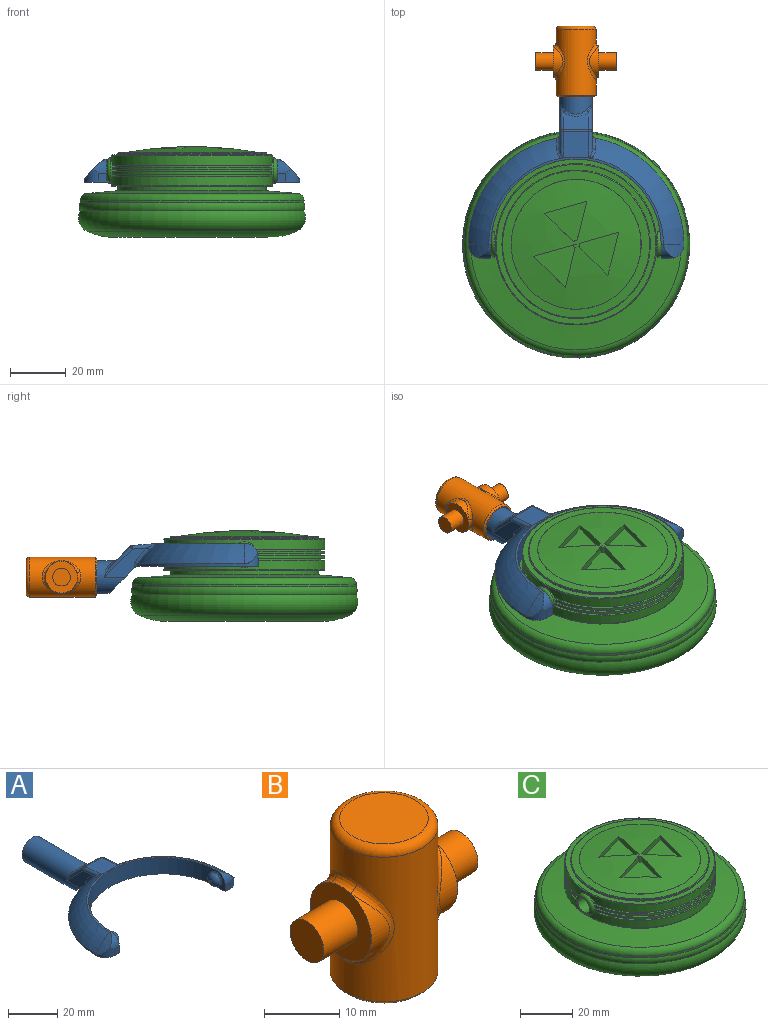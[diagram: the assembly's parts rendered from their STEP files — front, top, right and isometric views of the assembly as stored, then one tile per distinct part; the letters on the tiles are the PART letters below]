
ASSEMBLY  parts=3 mates=2
PART A: 48 faces, bbox 77.3x80.8x18.2 mm
  f0: plane 11.99x9.83mm, normal (0,-0.71,-0.71), area 141.5mm2, adj f1,f2,f9,f30,f43,f46
  f1: plane 15.39x10.49mm, normal (-1,0,0), area 63.5mm2, adj f0,f30,f32,f36,f46,f47
  f2: plane 15.39x10.49mm, normal (1,0,0), area 63.5mm2, adj f0,f30,f34,f39,f43,f44
  f3: plane 9.14x6.37mm, normal (0,0.71,0.71), area 67.6mm2, adj f35,f36,f39,f40
  f4: cylinder r=38.61mm len=37.99mm, axis (0,0,-1), area 42.6mm2, adj f6,f9,f17,f46,f47
  f5: torus R=19.3mm, axis (0,0,-1), area 507.8mm2, adj f10,f11,f12,f29,f42,f44
  f6: torus R=19.3mm, axis (0,0,-1), area 507.8mm2, adj f4,f11,f15,f28,f45,f47
  f7: cylinder r=30.48mm len=60.96mm, axis (0,0,-1), area 746.6mm2, adj f8,f9,f11,f14,f21,f24
  f8: plane 8.13x5.08mm, normal (-1,0,0), area 19.9mm2, adj f7,f9,f13,f19,f24
  f9: plane 77.22x43.73mm, normal (0,0,-1), area 956.2mm2, adj f0,f4,f7,f8,f10,f13,f14,f16
  f10: cylinder r=38.61mm len=37.99mm, axis (0,0,-1), area 42.6mm2, adj f5,f9,f20,f43,f44
  f11: plane 62.55x30.95mm, normal (0,0,1), area 75mm2, adj f5,f6,f7,f18,f19,f27
  f12: cylinder r=22.71mm len=7.33mm, axis (0,1,0), area 24.8mm2, adj f5,f19,f20
  f13: plane 3.05x3.05mm, normal (0,-1,0), area 9.3mm2, adj f8,f9,f19,f20
  f14: plane 8.13x5.08mm, normal (1,0,0), area 19.9mm2, adj f7,f9,f16,f18,f21
  f15: cylinder r=22.71mm len=7.33mm, axis (0,1,0), area 24.8mm2, adj f6,f17,f18
  f16: plane 3.05x3.05mm, normal (0,-1,0), area 9.3mm2, adj f9,f14,f17,f18
  f17: cylinder r=5.08mm len=5.08mm, axis (0,0,-1), area 21.9mm2, adj f4,f9,f15,f16,f18
  f18: cylinder r=5.08mm len=5.08mm, axis (-1,0,0), area 21.9mm2, adj f11,f14,f15,f16,f17
  f19: cylinder r=5.08mm len=5.08mm, axis (-1,0,0), area 21.9mm2, adj f8,f11,f12,f13,f20
  f20: cylinder r=5.08mm len=5.08mm, axis (0,0,-1), area 21.9mm2, adj f9,f10,f12,f13,f19
  f21: cylinder r=3.17mm len=6.35mm, axis (-1,0,0), area 12.7mm2, adj f7,f14,f23
  f22: plane 1.27x1.27mm, normal (1,0,0), area 1.3mm2, adj f23
  f23: torus R=0.64mm, axis (1,0,0), area 56.5mm2, adj f21,f22
  f24: cylinder r=3.17mm len=6.35mm, axis (1,0,0), area 12.7mm2, adj f7,f8,f26
  f25: plane 1.27x1.27mm, normal (-1,0,0), area 1.3mm2, adj f26
  f26: torus R=0.64mm, axis (-1,0,0), area 56.5mm2, adj f24,f25
  f27: plane 9.86x9.36mm, normal (0,0.09,1), area 85.6mm2, adj f11,f28,f29,f32,f34,f35,f42,f45
  f28: plane 1.04x0.17mm, normal (0,-1,0), area 0mm2, adj f6,f27,f45
  f29: plane 1.04x0.17mm, normal (0,-1,0), area 0mm2, adj f5,f27,f42
  f30: cylinder r=5.84mm len=33.01mm, axis (0,-1,0), area 1029.7mm2, adj f0,f1,f2,f31,f38,f40,f41
  f31: plane 11.68x11.68mm, normal (0,1,0), area 107.2mm2, adj f30
  f32: cylinder r=1.27mm len=9.13mm, axis (0,-1,0.09), area 14.4mm2, adj f1,f27,f33,f45
  f33: sphere r=1.27mm, area 1.5mm2, adj f32,f35,f36
  f34: cylinder r=1.27mm len=9.13mm, axis (0,1,-0.09), area 14.4mm2, adj f2,f27,f37,f42
  f35: cylinder r=1.27mm len=9.14mm, axis (-1,0,0), area 8.1mm2, adj f3,f27,f33,f37
  f36: cylinder r=1.27mm len=10.91mm, axis (0,-0.71,0.71), area 23.1mm2, adj f1,f3,f33,f38
  f37: sphere r=1.27mm, area 1.5mm2, adj f34,f35,f39
  f38: bspline ~4.55x2.75mm, area 2.3mm2, adj f30,f36,f40
  f39: cylinder r=1.27mm len=10.91mm, axis (0,0.71,-0.71), area 23.1mm2, adj f2,f3,f37,f41
  f40: bspline ~9.14x2.56mm, area 10.7mm2, adj f3,f30,f38,f41
  f41: bspline ~5.23x3.53mm, area 2.3mm2, adj f30,f39,f40
  f42: bspline ~4.62x3.14mm, area 5.2mm2, adj f5,f27,f29,f34,f44
  f43: cylinder r=1.27mm len=1.74mm, axis (0,0,-1), area 1.9mm2, adj f0,f2,f9,f10,f44
  f44: bspline ~8.6x7.86mm, area 11.9mm2, adj f2,f5,f10,f42,f43
  f45: bspline ~4.62x3.14mm, area 5.2mm2, adj f6,f27,f28,f32,f47
  f46: cylinder r=1.27mm len=1.74mm, axis (0,0,-1), area 1.9mm2, adj f0,f1,f4,f9,f47
  f47: bspline ~8.6x7.86mm, area 11.9mm2, adj f1,f4,f6,f45,f46
PART B: 25 faces, bbox 28.9x15.5x25.4 mm
  f0: cylinder r=5.71mm len=10.81mm, axis (-1,0,0), area 26.2mm2, adj f5,f15
  f1: cylinder r=5.71mm len=10.81mm, axis (-1,0,0), area 26.2mm2, adj f8,f11
  f2: cylinder r=7.14mm len=23.5mm, axis (0,0,-1), area 763.2mm2, adj f9,f10,f11,f12,f13,f14,f15,f16
  f3: plane 11.75x11.75mm, normal (0,0,1), area 108.4mm2, adj f17
  f4: plane 13.02x13.02mm, normal (0,0,-1), area 16.3mm2, adj f22,f24
  f5: plane 11.46x11.46mm, normal (1,0,0), area 70.9mm2, adj f0,f6,f13,f16,f18
  f6: cylinder r=5.71mm len=10.81mm, axis (-1,0,0), area 26.2mm2, adj f5,f14
  f7: cylinder r=5.71mm len=10.81mm, axis (-1,0,0), area 26.2mm2, adj f8,f10
  f8: plane 11.46x11.46mm, normal (-1,0,0), area 70.9mm2, adj f1,f7,f9,f12,f20
  f9: bspline ~4.64x1.73mm, area 6.5mm2, adj f2,f8,f10,f11
  f10: bspline ~13.62x4.91mm, area 20.7mm2, adj f2,f7,f9,f12
  f11: bspline ~13.6x4.87mm, area 20.7mm2, adj f1,f2,f9,f12
  f12: bspline ~4.64x1.73mm, area 6.5mm2, adj f2,f8,f10,f11
  f13: bspline ~4.64x1.73mm, area 6.5mm2, adj f2,f5,f14,f15
  f14: bspline ~13.62x4.91mm, area 20.7mm2, adj f2,f6,f13,f16
  f15: bspline ~13.6x4.87mm, area 20.7mm2, adj f0,f2,f13,f16
  f16: bspline ~4.64x1.73mm, area 6.5mm2, adj f2,f5,f14,f15
  f17: torus R=5.87mm, axis (0,0,1), area 83.8mm2, adj f2,f3
  f18: cylinder r=3.17mm len=6.35mm, axis (-1,0,0), area 126.7mm2, adj f5,f19
  f19: plane 6.35x6.35mm, normal (1,0,0), area 31.7mm2, adj f18
  f20: cylinder r=3.17mm len=6.35mm, axis (1,0,0), area 126.7mm2, adj f8,f21
  f21: plane 6.35x6.35mm, normal (-1,0,0), area 31.7mm2, adj f20
  f22: cylinder r=6.1mm len=22.86mm, axis (0,0,-1), area 875.6mm2, adj f4,f23
  f23: plane 12.19x12.19mm, normal (0,0,-1), area 116.7mm2, adj f22
  f24: cone r=7.14mm half-angle=45deg, axis (0,0,1), area 38.5mm2, adj f2,f4
PART C: 64 faces, bbox 96.3x96.3x32.5 mm
  f0: cylinder r=28.87mm len=57.73mm, axis (0,0,-1), area 595.8mm2, adj f1,f2,f54,f55,f60
  f1: plane 57.13x24.71mm, normal (0,0,1), area 102.4mm2, adj f0,f6,f54,f55
  f2: plane 57.13x24.71mm, normal (0,0,1), area 102.4mm2, adj f0,f5,f54,f55
  f3: plane 57.06x24.48mm, normal (0,0,-1), area 101.8mm2, adj f5,f7,f54,f55
  f4: plane 57.06x24.48mm, normal (0,0,-1), area 101.8mm2, adj f6,f8,f54,f55
  f5: cylinder r=27.59mm len=54.55mm, axis (0,0,-1), area 49.6mm2, adj f2,f3,f54,f55
  f6: cylinder r=27.59mm len=54.55mm, axis (0,0,-1), area 49.6mm2, adj f1,f4,f54,f55
  f7: cylinder r=28.87mm len=57.06mm, axis (0,0,-1), area 75.7mm2, adj f3,f10,f54,f55
  f8: cylinder r=28.87mm len=57.06mm, axis (0,0,-1), area 75.7mm2, adj f4,f9,f54,f55
  f9: plane 57.01x24.31mm, normal (0,0,1), area 101.4mm2, adj f8,f14,f54,f55
  f10: plane 57.01x24.31mm, normal (0,0,1), area 101.4mm2, adj f7,f13,f54,f55
  f11: plane 57.01x24.3mm, normal (0,0,-1), area 101.4mm2, adj f14,f16,f54,f55
  f12: plane 57.01x24.3mm, normal (0,0,-1), area 101.4mm2, adj f13,f15,f54,f55
  f13: cylinder r=27.59mm len=54.43mm, axis (0,0,-1), area 49.2mm2, adj f10,f12,f54,f55
  f14: cylinder r=27.59mm len=54.43mm, axis (0,0,-1), area 49.2mm2, adj f9,f11,f54,f55
  f15: cylinder r=28.87mm len=57.06mm, axis (0,0,-1), area 80mm2, adj f12,f19,f54,f55
  f16: cylinder r=28.87mm len=57.06mm, axis (0,0,-1), area 80mm2, adj f11,f20,f54,f55
  f17: plane 57.13x24.71mm, normal (0,0,-1), area 102.4mm2, adj f22,f23,f54,f55
  f18: plane 57.13x24.71mm, normal (0,0,-1), area 102.4mm2, adj f21,f23,f54,f55
  f19: plane 57.06x24.48mm, normal (0,0,1), area 101.8mm2, adj f15,f21,f54,f55
  f20: plane 57.06x24.48mm, normal (0,0,1), area 101.8mm2, adj f16,f22,f54,f55
  f21: cylinder r=27.59mm len=54.55mm, axis (0,0,-1), area 49.6mm2, adj f18,f19,f54,f55
  f22: cylinder r=27.59mm len=54.55mm, axis (0,0,-1), area 49.6mm2, adj f17,f20,f54,f55
  f23: cylinder r=28.87mm len=57.73mm, axis (0,0,-1), area 595.8mm2, adj f17,f18,f54,f55,f61
  f24: sphere r=135.39mm, area 1385.3mm2, adj f38,f39,f40,f41,f43,f44,f45,f46
  f25: plane 39.35x39.35mm, normal (0,0,-1), area 1216.2mm2, adj f26
  f26: torus R=20.13mm, axis (0,0,-1), area 1430.4mm2, adj f25,f27
  f27: torus R=27.75mm, axis (0,0,-1), area 3543.7mm2, adj f26,f28
  f28: torus R=35.37mm, axis (0,0,-1), area 2180.8mm2, adj f27,f29
  f29: torus R=37.36mm, axis (0,0,-1), area 734.8mm2, adj f28,f30
  f30: cylinder r=40.07mm len=80.14mm, axis (0,0,-1), area 213.4mm2, adj f29,f34
  f31: cone r=26.58mm half-angle=85deg, axis (0,0,-1), area 2265.9mm2, adj f32,f34
  f32: cylinder r=26.58mm len=53.16mm, axis (0,0,-1), area 265.1mm2, adj f31,f33
  f33: plane 57.23x57.23mm, normal (0,0,-1), area 352.3mm2, adj f32,f60
  f34: torus R=37.53mm, axis (0,0,1), area 928.9mm2, adj f30,f31
  f35: cone r=26.58mm half-angle=87deg, axis (0,0,-1), area 477.5mm2, adj f62,f63
  f36: cylinder r=26.58mm len=53.16mm, axis (0,0,-1), area 92.3mm2, adj f37,f62
  f37: plane 57.23x57.23mm, normal (0,0,1), area 352.3mm2, adj f36,f61
  f38: cylinder r=1.27mm len=2.53mm, axis (0,0,1), area 3.4mm2, adj f24,f39,f41,f42
  f39: plane 14.16x3.57mm, normal (-0.97,0.24,0), area 32.2mm2, adj f24,f38,f40,f42
  f40: plane 15.27x4.33mm, normal (0.27,-0.96,0), area 28mm2, adj f24,f39,f41,f42
  f41: plane 10.48x10.17mm, normal (0.7,0.72,0), area 32.2mm2, adj f24,f38,f40,f42
  f42: plane 15.27x14.51mm, normal (0,0,1), area 108.3mm2, adj f38,f39,f40,f41
  f43: cylinder r=1.27mm len=2.53mm, axis (0,0,1), area 3.4mm2, adj f24,f44,f46,f47
  f44: plane 14.05x3.99mm, normal (0.27,-0.96,0), area 32.2mm2, adj f24,f43,f45,f47
  f45: plane 11.39x11.06mm, normal (0.7,0.72,0), area 28mm2, adj f24,f44,f46,f47
  f46: plane 14.16x3.57mm, normal (-0.97,0.24,0), area 32.2mm2, adj f24,f43,f45,f47
  f47: plane 15.05x14.96mm, normal (0,0,1), area 108.3mm2, adj f43,f44,f45,f46
  f48: plane 14.05x3.99mm, normal (0.27,-0.96,0), area 32.2mm2, adj f24,f49,f51,f52
  f49: cylinder r=1.27mm len=2.53mm, axis (0,0,1), area 3.4mm2, adj f24,f48,f50,f52
  f50: plane 10.48x10.17mm, normal (0.7,0.72,0), area 32.2mm2, adj f24,f49,f51,f52
  f51: plane 15.39x3.88mm, normal (-0.97,0.24,0), area 28mm2, adj f24,f48,f50,f52
  f52: plane 15.39x14.36mm, normal (0,0,1), area 108.3mm2, adj f48,f49,f50,f51
  f53: plane 6.6x6.6mm, normal (1,0,0), area 2.6mm2, adj f58,f59
  f54: cylinder r=4.57mm len=9.14mm, axis (-1,0,0), area 20.2mm2, adj f0,f1,f2,f3,f4,f5,f6,f7
  f55: cylinder r=4.57mm len=9.14mm, axis (-1,0,0), area 20.2mm2, adj f0,f1,f2,f3,f4,f5,f6,f7
  f56: plane 6.6x6.6mm, normal (-1,0,0), area 2.6mm2, adj f57,f59
  f57: torus R=3.3mm, axis (1,0,0), area 51.5mm2, adj f55,f56
  f58: torus R=3.3mm, axis (1,0,0), area 51.5mm2, adj f53,f54
  f59: cylinder r=3.17mm len=60.96mm, axis (1,0,0), area 1216.1mm2, adj f53,f56
  f60: torus R=28.61mm, axis (0,0,1), area 72.1mm2, adj f0,f33
  f61: torus R=28.61mm, axis (0,0,-1), area 72.1mm2, adj f23,f37
  f62: torus R=26.33mm, axis (0,0,1), area 64.2mm2, adj f35,f36
  f63: torus R=23.29mm, axis (0,0,1), area 4.5mm2, adj f24,f35
PLACE A t=(32.34,27.52,20.85)mm
PLACE B rot(axis=(-1,0,0),90deg) t=(32.34,80.3,16.88)mm
PLACE C t=(32.34,27.52,33.52)mm
MATE revolute A.f24 <-> C.f54  axis (-1,0,0) through (62.82,27.52,24.92)mm
MATE revolute B.f2 <-> A.f30  axis (0,-1,0) through (32.34,103.16,16.88)mm
